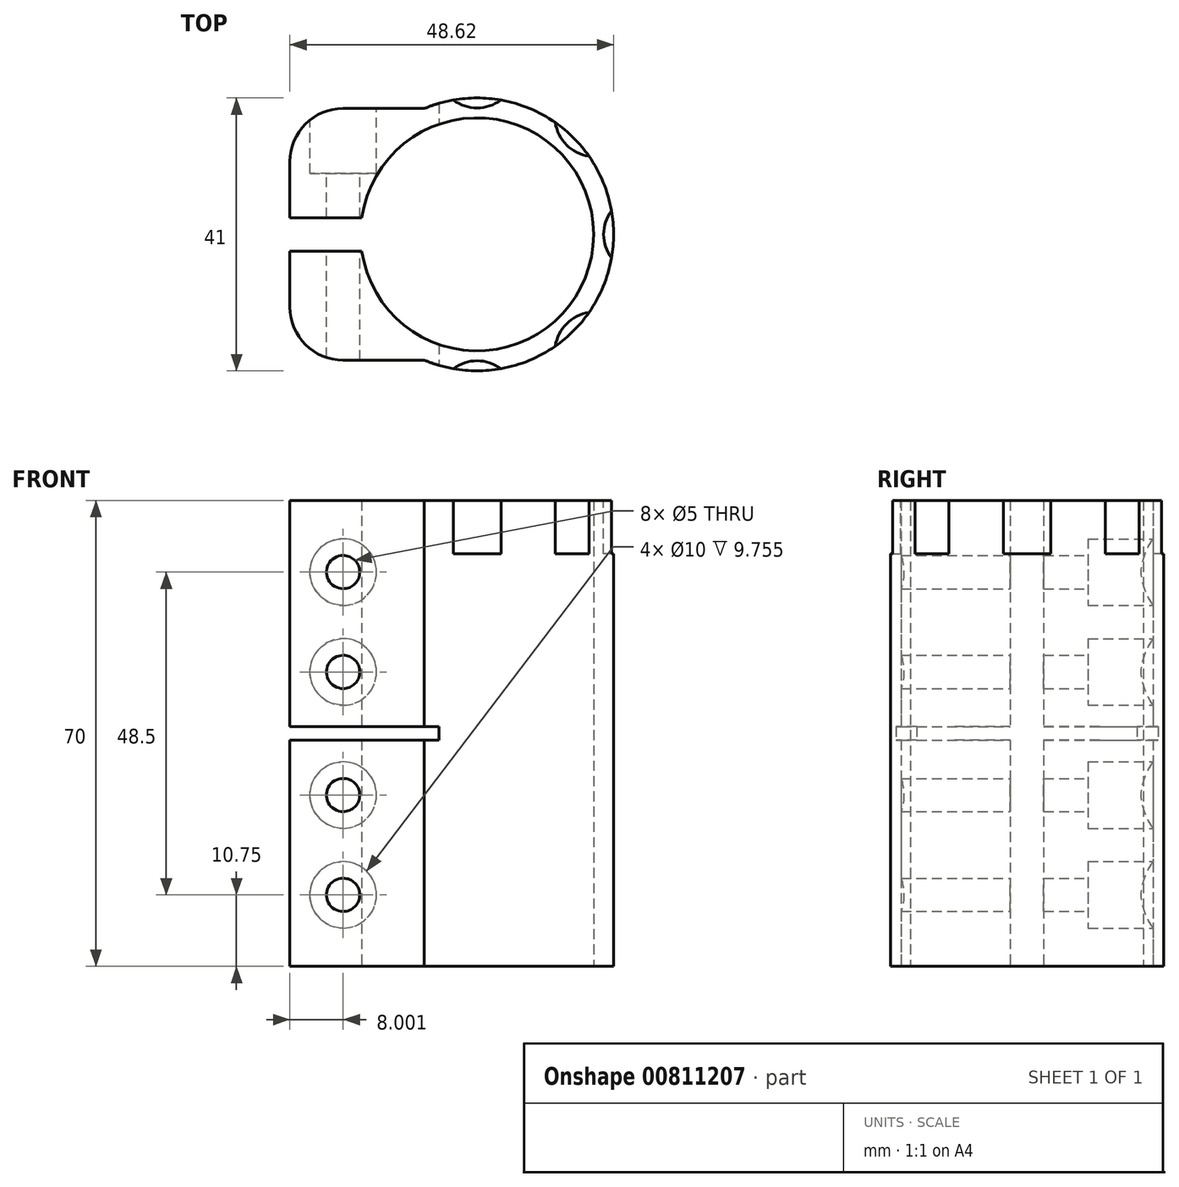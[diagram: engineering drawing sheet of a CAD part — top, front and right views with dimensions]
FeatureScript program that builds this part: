
annotation { "Feature Type Name" : "Feature", "Feature Type Description" : "" }
export const myFeature = defineFeature(function(context is Context, id is Id, definition is map)
    precondition{}
    {
        {
            var Q0;
            Q0=qCreatedBy(makeId("Top.planeOp"),FACE);
            var sketch = newSketch(context, id + "F0", { "sketchPlane" : qUnion([Q0])});
            skArc(sketch, "E0", {"start": v(-17.32, -2.5) * mm, "mid": v(17.5, 0) * mm, "end": v(-17.32, 2.5) * mm});
            skLineSegment(sketch, "E1", {"start": v(-17.32, 2.5) * mm, "end": v(-28.12, 2.5) * mm});
            skLineSegment(sketch, "E2", {"start": v(-28.12, 2.5) * mm, "end": v(-28.12, 10.9) * mm});
            skLineSegment(sketch, "E3", {"start": v(-20.12, 18.9) * mm, "end": v(-7.92, 18.9) * mm});
            skPoint(sketch, "E4.visualSharp", {"position": v(-28.12, 18.9) * mm});
            skArc(sketch, "E4.filletArc", {"start": v(-20.12, 18.9) * mm, "mid": v(-25.78, 16.57) * mm, "end": v(-28.12, 10.9) * mm});
            skLineSegment(sketch, "E5", {"start": v(0, 0) * mm, "end": v(44.16, 0) * mm, "construction": true});
            skLineSegment(sketch, "E6.MirrorCS", {"start": v(-20.12, -18.9) * mm, "end": v(-7.92, -18.9) * mm});
            skArc(sketch, "E7.MirrorCS", {"start": v(-20.12, -18.9) * mm, "mid": v(-25.78, -16.57) * mm, "end": v(-28.12, -10.9) * mm});
            skLineSegment(sketch, "E8.MirrorCS", {"start": v(-28.12, -2.5) * mm, "end": v(-28.12, -10.9) * mm});
            skLineSegment(sketch, "E9.MirrorCS", {"start": v(-17.32, -2.5) * mm, "end": v(-28.12, -2.5) * mm});
            skArc(sketch, "E10.trimOffspring", {"start": v(-7.92, -18.9) * mm, "mid": v(20.5, 0) * mm, "end": v(-7.92, 18.9) * mm});
            skSolve(sketch);
        }
        {
            var Q0;
            Q0=makeQuery(id+"F0.imprint","IMPRINT",FACE,{"disambiguationData":[TD([[makeQuery(id+"F0.imprint","IMPRINT",EDGE,{"derivedFrom":sQuery(id+"F0.wireOp",EDGE,"E0")}),-1.0]])]});
            extrude(context, id + "F1", {"entities" : qUnion([Q0]), "endBound" : BoundingType.SYMMETRIC, "depth" : 70 * mm, "offsetDistance" : 25 * mm});
        }
        {
            var Q0;
            Q0=makeQuery(id+"F1.opExtrude","SWEPT_FACE",FACE,{"disambiguationData":[OSD([sQuery(id+"F0.wireOp",EDGE,"E3")])]});
            var sketch = newSketch(context, id + "F2", { "sketchPlane" : qUnion([Q0])});
            skPoint(sketch, "E11", {"position": v(20.12, -24.25) * mm});
            skPoint(sketch, "E12", {"position": v(20.12, -9.25) * mm});
            skPoint(sketch, "E13", {"position": v(20.12, 9.25) * mm});
            skPoint(sketch, "E14", {"position": v(20.12, 24.25) * mm});
            skSolve(sketch);
        }
        {
            var Q0;
            Q0=sQuery(id+"F2.wireOp",VERTEX,"E11");
            var Q1;
            Q1=sQuery(id+"F2.wireOp",VERTEX,"E12");
            var Q2;
            Q2=sQuery(id+"F2.wireOp",VERTEX,"E13");
            var Q3;
            Q3=sQuery(id+"F2.wireOp",VERTEX,"E14");
            var Q4;
            Q4=makeQuery(id+"F1.opExtrude","SWEPT_BODY",BODY,{"disambiguationData":[OSD([sQuery(id+"F0.wireOp",EDGE,"E0"),sQuery(id+"F0.wireOp",EDGE,"E1"),sQuery(id+"F0.wireOp",EDGE,"E2"),sQuery(id+"F0.wireOp",EDGE,"E3"),sQuery(id+"F0.wireOp",EDGE,"E4.filletArc"),sQuery(id+"F0.wireOp",EDGE,"E6.MirrorCS"),sQuery(id+"F0.wireOp",EDGE,"E7.MirrorCS"),sQuery(id+"F0.wireOp",EDGE,"E8.MirrorCS"),sQuery(id+"F0.wireOp",EDGE,"E9.MirrorCS"),sQuery(id+"F0.wireOp",EDGE,"E10.trimOffspring")])]});
            hole(context, id + "F3", {"style" : HoleStyle.C_BORE, "endStyle" : HoleEndStyle.THROUGH, "holeDiameter" : 5 * mm, "cBoreDiameter" : 10 * mm, "cBoreDepth" : 8 * mm, "majorDiameter" : 5 * mm, "isTappedThrough" : true, "tappedDepth" : 12 * mm, "tapClearance" : 3, "locations" : qUnion([Q0, Q1, Q2, Q3]), "scope" : qUnion([Q4])});
        }
        {
            var Q0;
            Q0=qCreatedBy(makeId("Front.planeOp"),FACE);
            var sketch = newSketch(context, id + "F4", { "sketchPlane" : qUnion([Q0])});
            skLineSegment(sketch, "E15.bottom", {"start": v(-28.12, -1) * mm, "end": v(-5.72, -1) * mm});
            skLineSegment(sketch, "E15.top", {"start": v(-28.12, 1) * mm, "end": v(-5.72, 1) * mm});
            skLineSegment(sketch, "E15.left", {"start": v(-28.12, -1) * mm, "end": v(-28.12, 1) * mm});
            skLineSegment(sketch, "E15.right", {"start": v(-5.72, -1) * mm, "end": v(-5.72, 1) * mm});
            skSolve(sketch);
        }
        {
            var Q0;
            Q0=makeQuery(id+"F4.imprint","IMPRINT",FACE,{"disambiguationData":[TD([[makeQuery(id+"F4.imprint","IMPRINT",EDGE,{"derivedFrom":sQuery(id+"F4.wireOp",EDGE,"E15.bottom")}),1.0]])]});
            extrude(context, id + "F5", {"entities" : qUnion([Q0]), "operationType" : NewBodyOperationType.REMOVE, "endBound" : BoundingType.SYMMETRIC, "oppositeDirection" : true, "depth" : 50 * mm, "offsetDistance" : 25 * mm});
        }
        {
            var Q0;
            Q0=makeQuery(id+"F1.opExtrude","CAP_FACE",FACE,{"disambiguationData":[OSD([sQuery(id+"F0.wireOp",EDGE,"E0"),sQuery(id+"F0.wireOp",EDGE,"E1"),sQuery(id+"F0.wireOp",EDGE,"E2"),sQuery(id+"F0.wireOp",EDGE,"E3"),sQuery(id+"F0.wireOp",EDGE,"E4.filletArc"),sQuery(id+"F0.wireOp",EDGE,"E6.MirrorCS"),sQuery(id+"F0.wireOp",EDGE,"E7.MirrorCS"),sQuery(id+"F0.wireOp",EDGE,"E8.MirrorCS"),sQuery(id+"F0.wireOp",EDGE,"E9.MirrorCS"),sQuery(id+"F0.wireOp",EDGE,"E10.trimOffspring")])],"isStart":false});
            var sketch = newSketch(context, id + "F6", { "sketchPlane" : qUnion([Q0])});
            skCircle(sketch, "E16", {"center": v(0, -25) * mm, "radius": 6 * mm});
            skCircle(sketch, "E17.1.0", {"center": v(17.68, -17.68) * mm, "radius": 6 * mm});
            skCircle(sketch, "E17.2.0", {"center": v(25, 0) * mm, "radius": 6 * mm});
            skCircle(sketch, "E17.3.0", {"center": v(17.68, 17.68) * mm, "radius": 6 * mm});
            skCircle(sketch, "E17.4.0", {"center": v(0, 25) * mm, "radius": 6 * mm});
            skPoint(sketch, "E17.center", {"position": v(0, 0) * mm});
            skLineSegment(sketch, "E17.anchor1", {"start": v(0, 0) * mm, "end": v(0, -25) * mm, "construction": true});
            skLineSegment(sketch, "E17.anchor2", {"start": v(0, 0) * mm, "end": v(0, 25) * mm, "construction": true});
            skSolve(sketch);
        }
        {
            var Q0;
            {var subQ0=sQuery(id+"F6.wireOp",EDGE,"E17.4.0");var subQ1=makeQuery(id+"F1.opExtrude","CAP_EDGE",EDGE,{"disambiguationData":[OSD([sQuery(id+"F0.wireOp",EDGE,"E10.trimOffspring")])],"isStart":false});var subQ2=makeQuery(id+"F6.imprint","INTERSECT",VERTEX,{"disambiguationData":[OD(0.0)],"derivedFrom":[subQ1,subQ0]});Q0=makeQuery(id+"F6.imprint","IMPRINT",FACE,{"disambiguationData":[TD([[makeQuery(id+"F6.imprint","IMPRINT",EDGE,{"disambiguationData":[TD([[subQ2,1.0]])],"derivedFrom":subQ0}),1.0]])]});}
            var Q1;
            {var subQ0=sQuery(id+"F6.wireOp",EDGE,"E17.3.0");var subQ1=makeQuery(id+"F1.opExtrude","CAP_EDGE",EDGE,{"disambiguationData":[OSD([sQuery(id+"F0.wireOp",EDGE,"E10.trimOffspring")])],"isStart":false});var subQ2=makeQuery(id+"F6.imprint","INTERSECT",VERTEX,{"disambiguationData":[OD(0.0)],"derivedFrom":[subQ1,subQ0]});Q1=makeQuery(id+"F6.imprint","IMPRINT",FACE,{"disambiguationData":[TD([[makeQuery(id+"F6.imprint","IMPRINT",EDGE,{"disambiguationData":[TD([[subQ2,1.0]])],"derivedFrom":subQ0}),1.0]])]});}
            var Q2;
            {var subQ0=sQuery(id+"F6.wireOp",EDGE,"E17.4.0");var subQ1=makeQuery(id+"F1.opExtrude","CAP_EDGE",EDGE,{"disambiguationData":[OSD([sQuery(id+"F0.wireOp",EDGE,"E10.trimOffspring")])],"isStart":false});var subQ2=makeQuery(id+"F6.imprint","INTERSECT",VERTEX,{"disambiguationData":[OD(0.0)],"derivedFrom":[subQ1,subQ0]});Q2=makeQuery(id+"F6.imprint","IMPRINT",FACE,{"disambiguationData":[TD([[makeQuery(id+"F6.imprint","IMPRINT",EDGE,{"disambiguationData":[TD([[subQ2,-1.0]])],"derivedFrom":subQ0}),1.0]])]});}
            var Q3;
            {var subQ0=sQuery(id+"F6.wireOp",EDGE,"E17.3.0");var subQ1=makeQuery(id+"F1.opExtrude","CAP_EDGE",EDGE,{"disambiguationData":[OSD([sQuery(id+"F0.wireOp",EDGE,"E10.trimOffspring")])],"isStart":false});var subQ2=makeQuery(id+"F6.imprint","INTERSECT",VERTEX,{"disambiguationData":[OD(0.0)],"derivedFrom":[subQ1,subQ0]});Q3=makeQuery(id+"F6.imprint","IMPRINT",FACE,{"disambiguationData":[TD([[makeQuery(id+"F6.imprint","IMPRINT",EDGE,{"disambiguationData":[TD([[subQ2,-1.0]])],"derivedFrom":subQ0}),1.0]])]});}
            var Q4;
            {var subQ0=sQuery(id+"F6.wireOp",EDGE,"E17.2.0");var subQ1=makeQuery(id+"F1.opExtrude","CAP_EDGE",EDGE,{"disambiguationData":[OSD([sQuery(id+"F0.wireOp",EDGE,"E10.trimOffspring")])],"isStart":false});var subQ2=makeQuery(id+"F6.imprint","INTERSECT",VERTEX,{"disambiguationData":[OD(0.0)],"derivedFrom":[subQ1,subQ0]});Q4=makeQuery(id+"F6.imprint","IMPRINT",FACE,{"disambiguationData":[TD([[makeQuery(id+"F6.imprint","IMPRINT",EDGE,{"disambiguationData":[TD([[subQ2,-1.0]])],"derivedFrom":subQ0}),1.0]])]});}
            var Q5;
            {var subQ0=sQuery(id+"F6.wireOp",EDGE,"E17.2.0");var subQ1=makeQuery(id+"F1.opExtrude","CAP_EDGE",EDGE,{"disambiguationData":[OSD([sQuery(id+"F0.wireOp",EDGE,"E10.trimOffspring")])],"isStart":false});var subQ2=makeQuery(id+"F6.imprint","INTERSECT",VERTEX,{"disambiguationData":[OD(0.0)],"derivedFrom":[subQ1,subQ0]});Q5=makeQuery(id+"F6.imprint","IMPRINT",FACE,{"disambiguationData":[TD([[makeQuery(id+"F6.imprint","IMPRINT",EDGE,{"disambiguationData":[TD([[subQ2,1.0]])],"derivedFrom":subQ0}),1.0]])]});}
            var Q6;
            {var subQ0=sQuery(id+"F6.wireOp",EDGE,"E17.1.0");var subQ1=makeQuery(id+"F1.opExtrude","CAP_EDGE",EDGE,{"disambiguationData":[OSD([sQuery(id+"F0.wireOp",EDGE,"E10.trimOffspring")])],"isStart":false});var subQ2=makeQuery(id+"F6.imprint","INTERSECT",VERTEX,{"disambiguationData":[OD(0.0)],"derivedFrom":[subQ1,subQ0]});Q6=makeQuery(id+"F6.imprint","IMPRINT",FACE,{"disambiguationData":[TD([[makeQuery(id+"F6.imprint","IMPRINT",EDGE,{"disambiguationData":[TD([[subQ2,-1.0]])],"derivedFrom":subQ0}),1.0]])]});}
            var Q7;
            {var subQ0=sQuery(id+"F6.wireOp",EDGE,"E16");var subQ1=makeQuery(id+"F1.opExtrude","CAP_EDGE",EDGE,{"disambiguationData":[OSD([sQuery(id+"F0.wireOp",EDGE,"E10.trimOffspring")])],"isStart":false});var subQ2=makeQuery(id+"F6.imprint","INTERSECT",VERTEX,{"disambiguationData":[OD(0.0)],"derivedFrom":[subQ1,subQ0]});Q7=makeQuery(id+"F6.imprint","IMPRINT",FACE,{"disambiguationData":[TD([[makeQuery(id+"F6.imprint","IMPRINT",EDGE,{"disambiguationData":[TD([[subQ2,-1.0]])],"derivedFrom":subQ0}),1.0]])]});}
            var Q8;
            {var subQ0=sQuery(id+"F6.wireOp",EDGE,"E17.1.0");var subQ1=makeQuery(id+"F1.opExtrude","CAP_EDGE",EDGE,{"disambiguationData":[OSD([sQuery(id+"F0.wireOp",EDGE,"E10.trimOffspring")])],"isStart":false});var subQ2=makeQuery(id+"F6.imprint","INTERSECT",VERTEX,{"disambiguationData":[OD(0.0)],"derivedFrom":[subQ1,subQ0]});Q8=makeQuery(id+"F6.imprint","IMPRINT",FACE,{"disambiguationData":[TD([[makeQuery(id+"F6.imprint","IMPRINT",EDGE,{"disambiguationData":[TD([[subQ2,1.0]])],"derivedFrom":subQ0}),1.0]])]});}
            var Q9;
            {var subQ0=sQuery(id+"F6.wireOp",EDGE,"E16");var subQ1=makeQuery(id+"F1.opExtrude","CAP_EDGE",EDGE,{"disambiguationData":[OSD([sQuery(id+"F0.wireOp",EDGE,"E10.trimOffspring")])],"isStart":false});var subQ2=makeQuery(id+"F6.imprint","INTERSECT",VERTEX,{"disambiguationData":[OD(0.0)],"derivedFrom":[subQ1,subQ0]});Q9=makeQuery(id+"F6.imprint","IMPRINT",FACE,{"disambiguationData":[TD([[makeQuery(id+"F6.imprint","IMPRINT",EDGE,{"disambiguationData":[TD([[subQ2,1.0]])],"derivedFrom":subQ0}),1.0]])]});}
            extrude(context, id + "F7", {"entities" : qUnion([Q0, Q1, Q2, Q3, Q4, Q5, Q6, Q7, Q8, Q9]), "operationType" : NewBodyOperationType.REMOVE, "oppositeDirection" : true, "depth" : 8 * mm, "offsetDistance" : 25 * mm});
        }
    });
